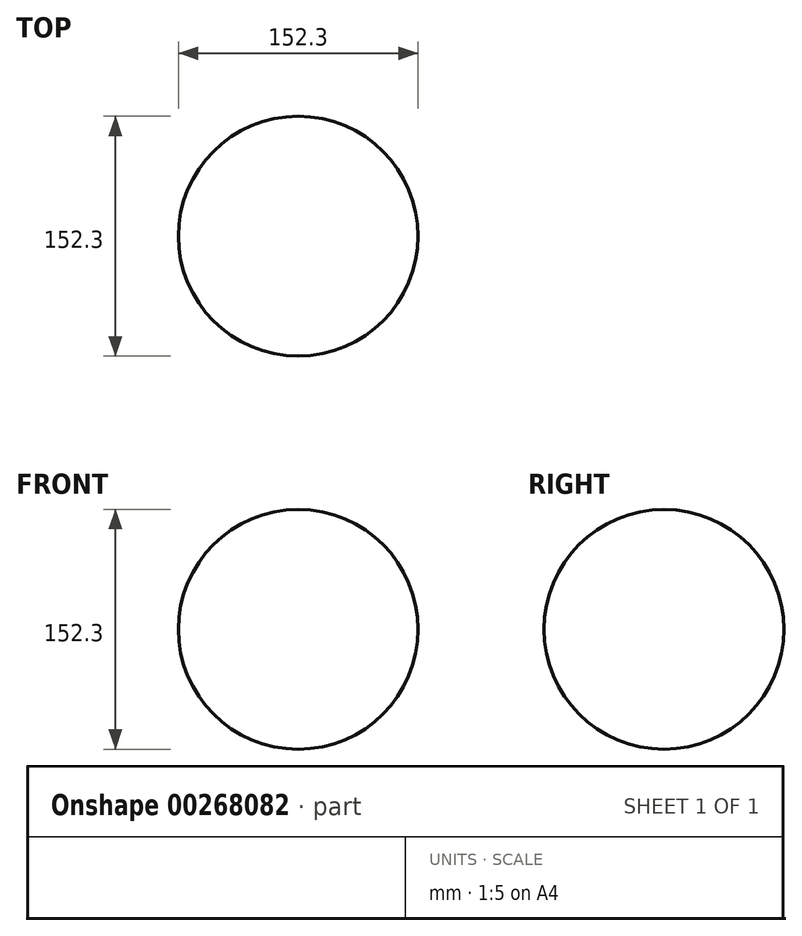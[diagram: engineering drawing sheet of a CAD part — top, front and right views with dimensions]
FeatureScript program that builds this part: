
annotation { "Feature Type Name" : "Feature", "Feature Type Description" : "" }
export const myFeature = defineFeature(function(context is Context, id is Id, definition is map)
    precondition{}
    {
        {
            var Q0;
            Q0=qCreatedBy(makeId("Front.planeOp"),FACE);
            var sketch = newSketch(context, id + "F0", { "sketchPlane" : qUnion([Q0])});
            skCircle(sketch, "E0", {"center": v(0, 0) * mm, "radius": 76.15 * mm});
            skLineSegment(sketch, "E1", {"start": v(0, 76.15) * mm, "end": v(0, -76.15) * mm});
            skSolve(sketch);
        }
        {
            var Q0;
            {var subQ0=sQuery(id+"F0.wireOp",EDGE,"E1");Q0=makeQuery(id+"F0.imprint","IMPRINT",FACE,{"disambiguationData":[TD([[makeQuery(id+"F0.imprint","IMPRINT",EDGE,{"derivedFrom":subQ0}),-1.0]])]});}
            var Q1;
            Q1=sQuery(id+"F0.wireOp",EDGE,"E1");
            revolve(context, id + "F1", {"entities" : qUnion([Q0]), "axis" : qUnion([Q1]), "revolveType" : RevolveType.FULL});
        }
    });
